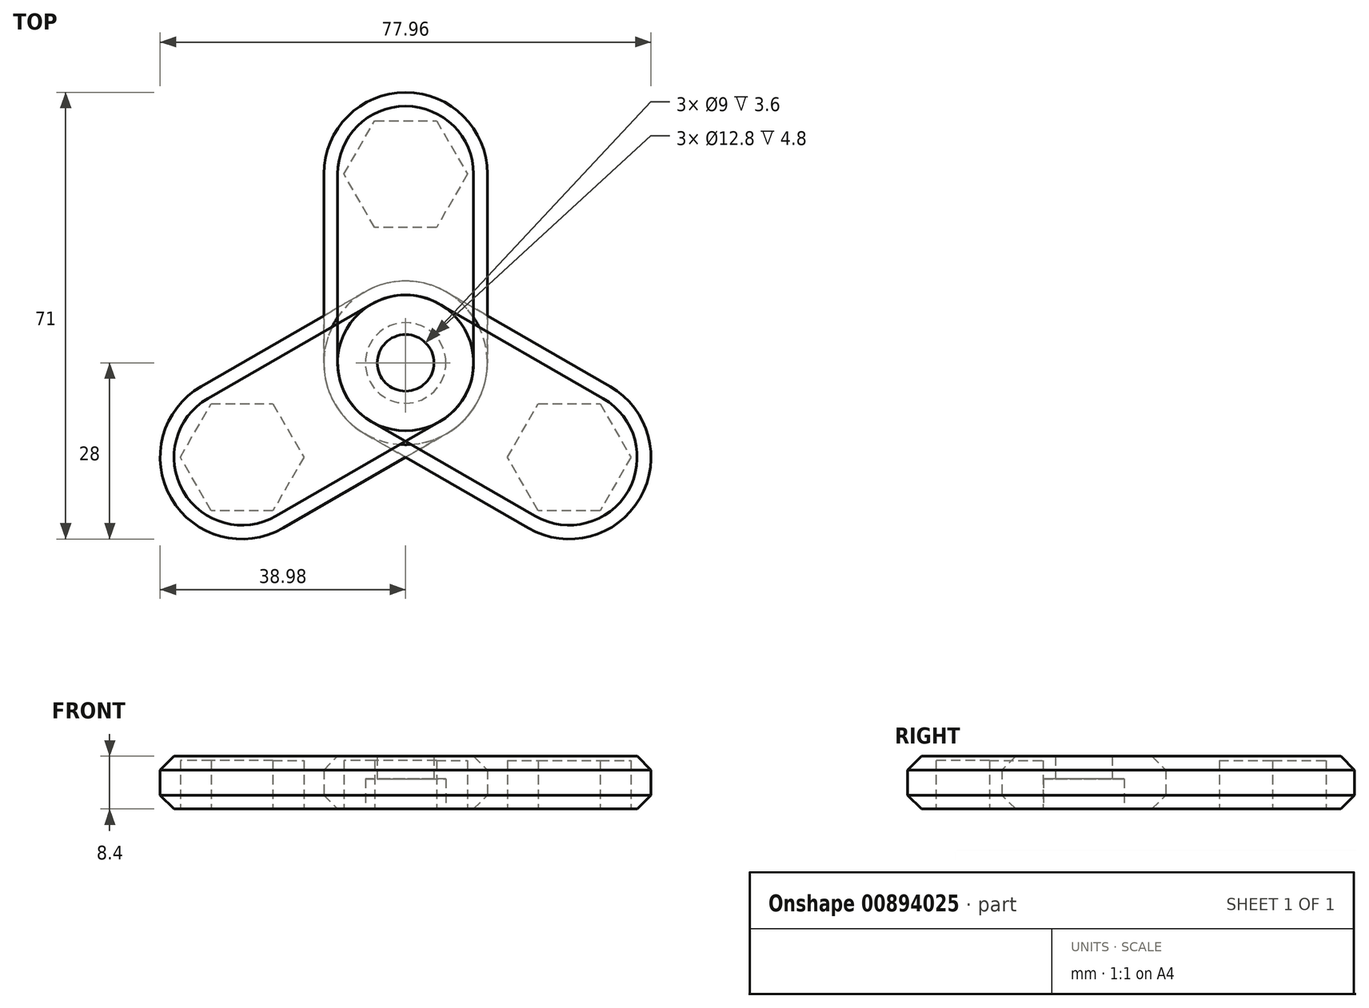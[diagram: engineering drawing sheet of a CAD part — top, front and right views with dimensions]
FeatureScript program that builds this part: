
annotation { "Feature Type Name" : "Feature", "Feature Type Description" : "" }
export const myFeature = defineFeature(function(context is Context, id is Id, definition is map)
    precondition{}
    {
        {
            var Q0;
            Q0=qCreatedBy(makeId("Top.planeOp"),FACE);
            var sketch = newSketch(context, id + "F0", { "sketchPlane" : qUnion([Q0])});
            skCircle(sketch, "E0", {"center": v(0, 0) * mm, "radius": 13 * mm});
            skCircle(sketch, "E1", {"center": v(0, 0) * mm, "radius": 6.4 * mm});
            skCircle(sketch, "E2", {"center": v(0, 30) * mm, "radius": 13 * mm});
            skCircle(sketch, "E3.cCircle", {"center": v(0, 30) * mm, "radius": 8.5 * mm, "construction": true});
            skLineSegment(sketch, "E3.0", {"start": v(9.81, 30) * mm, "end": v(4.9, 21.5) * mm});
            skLineSegment(sketch, "E3.1", {"start": v(4.9, 21.5) * mm, "end": v(-4.9, 21.5) * mm});
            skLineSegment(sketch, "E3.2", {"start": v(-4.9, 21.5) * mm, "end": v(-9.81, 30) * mm});
            skLineSegment(sketch, "E3.3", {"start": v(-9.81, 30) * mm, "end": v(-4.9, 38.5) * mm});
            skLineSegment(sketch, "E3.4", {"start": v(-4.9, 38.5) * mm, "end": v(4.9, 38.5) * mm});
            skLineSegment(sketch, "E3.5", {"start": v(4.9, 38.5) * mm, "end": v(9.81, 30) * mm});
            skPoint(sketch, "E3.0.midPoint", {"position": v(7.36, 25.75) * mm});
            skCircle(sketch, "E4", {"center": v(0, 0) * mm, "radius": 4.5 * mm});
            skLineSegment(sketch, "E5", {"start": v(-13, 0) * mm, "end": v(-13, 30) * mm});
            skLineSegment(sketch, "E6", {"start": v(13, 0) * mm, "end": v(13, 30) * mm});
            skSolve(sketch);
        }
        {
            var Q0;
            {var subQ0=sQuery(id+"F0.wireOp",EDGE,"E5");Q0=makeQuery(id+"F0.imprint","IMPRINT",FACE,{"disambiguationData":[TD([[makeQuery(id+"F0.imprint","IMPRINT",EDGE,{"derivedFrom":subQ0}),-1.0]])]});}
            var Q1;
            Q1=makeQuery(id+"F0.imprint","IMPRINT",FACE,{"disambiguationData":[TD([[makeQuery(id+"F0.imprint","IMPRINT",EDGE,{"derivedFrom":sQuery(id+"F0.wireOp",EDGE,"E3.0")}),1.0]])]});
            var Q2;
            Q2=makeQuery(id+"F0.imprint","IMPRINT",FACE,{"disambiguationData":[TD([[makeQuery(id+"F0.imprint","IMPRINT",EDGE,{"derivedFrom":sQuery(id+"F0.wireOp",EDGE,"E3.0")}),-1.0]])]});
            var Q3;
            Q3=makeQuery(id+"F0.imprint","IMPRINT",FACE,{"disambiguationData":[TD([[makeQuery(id+"F0.imprint","IMPRINT",EDGE,{"derivedFrom":sQuery(id+"F0.wireOp",EDGE,"E1")}),-1.0]])]});
            var Q4;
            Q4=makeQuery(id+"F0.imprint","IMPRINT",FACE,{"disambiguationData":[TD([[makeQuery(id+"F0.imprint","IMPRINT",EDGE,{"derivedFrom":sQuery(id+"F0.wireOp",EDGE,"E1")}),1.0]])]});
            extrude(context, id + "F1", {"entities" : qUnion([Q0, Q1, Q2, Q3, Q4]), "depth" : 7.7 * mm, "offsetDistance" : 25 * mm});
        }
        {
            var Q0;
            Q0=makeQuery(id+"F0.imprint","IMPRINT",FACE,{"disambiguationData":[TD([[makeQuery(id+"F0.imprint","IMPRINT",EDGE,{"derivedFrom":sQuery(id+"F0.wireOp",EDGE,"E3.0")}),-1.0]])]});
            extrude(context, id + "F2", {"entities" : qUnion([Q0]), "operationType" : NewBodyOperationType.REMOVE, "depth" : 7.9 * mm, "offsetDistance" : 25 * mm});
        }
        {
            var Q0;
            Q0=makeQuery(id+"F0.imprint","IMPRINT",FACE,{"disambiguationData":[TD([[makeQuery(id+"F0.imprint","IMPRINT",EDGE,{"derivedFrom":sQuery(id+"F0.wireOp",EDGE,"E1")}),1.0]])]});
            extrude(context, id + "F3", {"entities" : qUnion([Q0]), "operationType" : NewBodyOperationType.REMOVE, "depth" : 4.8 * mm, "offsetDistance" : 25 * mm});
        }
        {
            var Q0;
            Q0=makeQuery(id+"F0.imprint","IMPRINT",FACE,{"disambiguationData":[TD([[makeQuery(id+"F0.imprint","IMPRINT",EDGE,{"derivedFrom":sQuery(id+"F0.wireOp",EDGE,"E1")}),1.0]])]});
            var Q1;
            Q1=makeQuery(id+"F0.imprint","IMPRINT",FACE,{"disambiguationData":[TD([[makeQuery(id+"F0.imprint","IMPRINT",EDGE,{"derivedFrom":sQuery(id+"F0.wireOp",EDGE,"E1")}),-1.0]])]});
            var Q2;
            {var subQ0=sQuery(id+"F0.wireOp",EDGE,"E5");Q2=makeQuery(id+"F0.imprint","IMPRINT",FACE,{"disambiguationData":[TD([[makeQuery(id+"F0.imprint","IMPRINT",EDGE,{"derivedFrom":subQ0}),-1.0]])]});}
            var Q3;
            Q3=makeQuery(id+"F0.imprint","IMPRINT",FACE,{"disambiguationData":[TD([[makeQuery(id+"F0.imprint","IMPRINT",EDGE,{"derivedFrom":sQuery(id+"F0.wireOp",EDGE,"E3.0")}),1.0]])]});
            var Q4;
            Q4=makeQuery(id+"F0.imprint","IMPRINT",FACE,{"disambiguationData":[TD([[makeQuery(id+"F0.imprint","IMPRINT",EDGE,{"derivedFrom":sQuery(id+"F0.wireOp",EDGE,"E3.0")}),-1.0]])]});
            extrude(context, id + "F4", {"entities" : qUnion([Q0, Q1, Q2, Q3, Q4]), "operationType" : NewBodyOperationType.ADD, "depth" : 8.4 * mm, "offsetDistance" : 25 * mm, "hasSecondDirection" : true, "secondDirectionOppositeDirection" : false, "secondDirectionDepth" : 7.7 * mm});
        }
        {
            var Q0;
            Q0=makeQuery(id+"F1.opExtrude","SWEPT_BODY",BODY,{"disambiguationData":[OSD([sQuery(id+"F0.wireOp",EDGE,"E0"),sQuery(id+"F0.wireOp",EDGE,"E2"),sQuery(id+"F0.wireOp",EDGE,"E4"),sQuery(id+"F0.wireOp",EDGE,"E5"),sQuery(id+"F0.wireOp",EDGE,"E6")])]});
            var Q1;
            Q1=makeQuery(id+"F3.boolean.opBoolean","COPY",FACE,{"derivedFrom":makeQuery(id+"F3.opExtrude","SWEPT_FACE",FACE,{"disambiguationData":[OSD([sQuery(id+"F0.wireOp",EDGE,"E1")])]})});
            circularPattern(context, id + "F5", {"entities" : qUnion([Q0]), "axis" : qUnion([Q1]), "angle" : 360 * degree, "instanceCount" : 3, "equalSpace" : true});
        }
        {
            var Q0;
            Q0=makeQuery(id+"F5.opPattern","COPY",EDGE,{"derivedFrom":makeQuery(id+"F1.opExtrude","CAP_EDGE",EDGE,{"disambiguationData":[OSD([sQuery(id+"F0.wireOp",EDGE,"E5")])],"isStart":true}),"instanceName":"2"});
            var Q1;
            Q1=makeQuery(id+"F5.opPattern","COPY",EDGE,{"derivedFrom":makeQuery(id+"F1.opExtrude","CAP_EDGE",EDGE,{"disambiguationData":[OSD([sQuery(id+"F0.wireOp",EDGE,"E2")])],"isStart":true}),"instanceName":"2"});
            var Q2;
            Q2=makeQuery(id+"F5.opPattern","COPY",EDGE,{"derivedFrom":makeQuery(id+"F1.opExtrude","CAP_EDGE",EDGE,{"disambiguationData":[OSD([sQuery(id+"F0.wireOp",EDGE,"E6")])],"isStart":true}),"instanceName":"2"});
            var Q3;
            Q3=makeQuery(id+"F5.opPattern","COPY",EDGE,{"derivedFrom":makeQuery(id+"F1.opExtrude","CAP_EDGE",EDGE,{"disambiguationData":[OSD([sQuery(id+"F0.wireOp",EDGE,"E5")])],"isStart":true}),"instanceName":"1"});
            var Q4;
            Q4=makeQuery(id+"F5.opPattern","COPY",EDGE,{"derivedFrom":makeQuery(id+"F1.opExtrude","CAP_EDGE",EDGE,{"disambiguationData":[OSD([sQuery(id+"F0.wireOp",EDGE,"E2")])],"isStart":true}),"instanceName":"1"});
            var Q5;
            Q5=makeQuery(id+"F5.opPattern","COPY",EDGE,{"derivedFrom":makeQuery(id+"F1.opExtrude","CAP_EDGE",EDGE,{"disambiguationData":[OSD([sQuery(id+"F0.wireOp",EDGE,"E6")])],"isStart":true}),"instanceName":"1"});
            var Q6;
            Q6=makeQuery(id+"F1.opExtrude","CAP_EDGE",EDGE,{"disambiguationData":[OSD([sQuery(id+"F0.wireOp",EDGE,"E5")])],"isStart":true});
            var Q7;
            Q7=makeQuery(id+"F1.opExtrude","CAP_EDGE",EDGE,{"disambiguationData":[OSD([sQuery(id+"F0.wireOp",EDGE,"E6")])],"isStart":true});
            var Q8;
            Q8=makeQuery(id+"F1.opExtrude","CAP_EDGE",EDGE,{"disambiguationData":[OSD([sQuery(id+"F0.wireOp",EDGE,"E2")])],"isStart":true});
            var Q9;
            Q9=makeQuery(id+"F1.opExtrude","CAP_EDGE",EDGE,{"disambiguationData":[OSD([sQuery(id+"F0.wireOp",EDGE,"E6")])],"isStart":false});
            var Q10;
            Q10=makeQuery(id+"F5.opPattern","COPY",EDGE,{"derivedFrom":makeQuery(id+"F1.opExtrude","CAP_EDGE",EDGE,{"disambiguationData":[OSD([sQuery(id+"F0.wireOp",EDGE,"E5")])],"isStart":false}),"instanceName":"2"});
            var Q11;
            Q11=makeQuery(id+"F5.opPattern","COPY",EDGE,{"derivedFrom":makeQuery(id+"F1.opExtrude","CAP_EDGE",EDGE,{"disambiguationData":[OSD([sQuery(id+"F0.wireOp",EDGE,"E5")])],"isStart":false}),"instanceName":"1"});
            var Q12;
            Q12=makeQuery(id+"F4.opExtrude","CAP_EDGE",EDGE,{"disambiguationData":[OSD([sQuery(id+"F0.wireOp",EDGE,"E6")])],"isStart":false});
            var Q13;
            Q13=makeQuery(id+"F5.opPattern","COPY",EDGE,{"derivedFrom":makeQuery(id+"F4.opExtrude","CAP_EDGE",EDGE,{"disambiguationData":[OSD([sQuery(id+"F0.wireOp",EDGE,"E5")])],"isStart":false}),"instanceName":"2"});
            var Q14;
            Q14=makeQuery(id+"F5.opPattern","COPY",EDGE,{"derivedFrom":makeQuery(id+"F4.opExtrude","CAP_EDGE",EDGE,{"disambiguationData":[OSD([sQuery(id+"F0.wireOp",EDGE,"E5")])],"isStart":false}),"instanceName":"1"});
            chamfer(context, id + "F6", {"entities" : qUnion([Q0, Q1, Q2, Q3, Q4, Q5, Q6, Q7, Q8, Q9, Q10, Q11, Q12, Q13, Q14]), "width" : 2.2 * mm, "tangentPropagation" : true});
        }
    });
